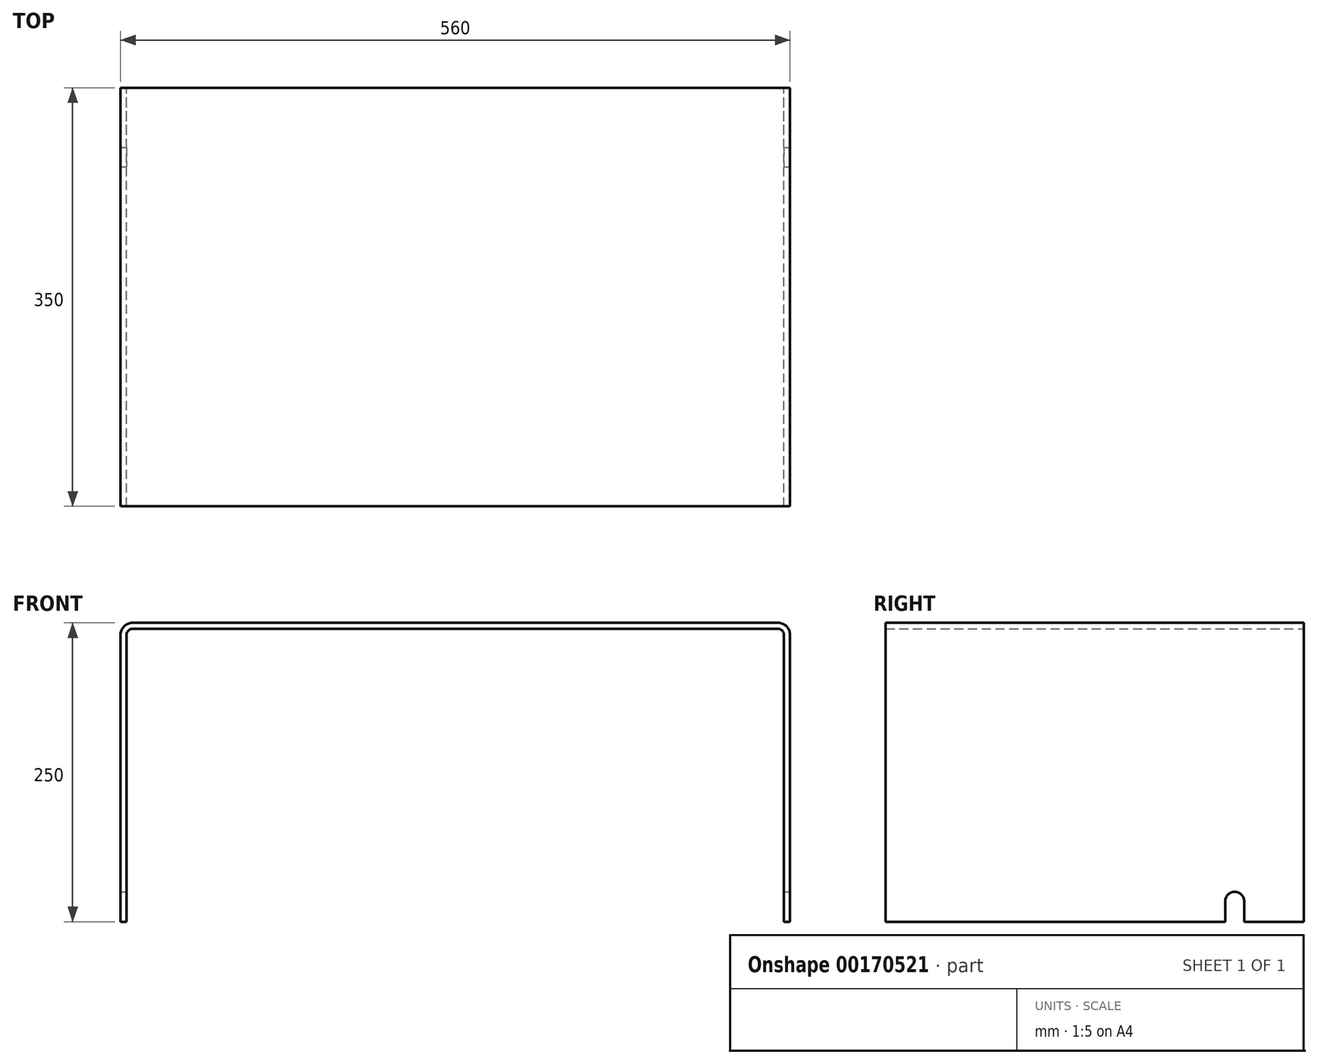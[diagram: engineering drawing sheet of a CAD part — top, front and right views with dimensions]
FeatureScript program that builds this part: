
annotation { "Feature Type Name" : "Feature", "Feature Type Description" : "" }
export const myFeature = defineFeature(function(context is Context, id is Id, definition is map)
    precondition{}
    {
        {
            var Q0;
            Q0=qCreatedBy(makeId("Front.planeOp"),FACE);
            var sketch = newSketch(context, id + "F0", { "sketchPlane" : qUnion([Q0])});
            skLineSegment(sketch, "E0.bottom", {"start": v(-270, 138.08) * mm, "end": v(270, 138.08) * mm});
            skLineSegment(sketch, "E0.top", {"start": v(-280, -111.92) * mm, "end": v(-275, -111.92) * mm});
            skLineSegment(sketch, "E0.left", {"start": v(-280, 128.08) * mm, "end": v(-280, -111.92) * mm});
            skLineSegment(sketch, "E0.right", {"start": v(280, 128.08) * mm, "end": v(280, -111.92) * mm});
            skLineSegment(sketch, "E1", {"start": v(-394.49, 0) * mm, "end": v(397.92, 0) * mm, "construction": true});
            skLineSegment(sketch, "E2", {"start": v(0, 473.58) * mm, "end": v(0, -448.6) * mm, "construction": true});
            skPoint(sketch, "E3.visualSharp", {"position": v(-280, 138.08) * mm});
            skArc(sketch, "E3.filletArc", {"start": v(-270, 138.08) * mm, "mid": v(-277.07, 135.15) * mm, "end": v(-280, 128.08) * mm});
            skPoint(sketch, "E4.visualSharp", {"position": v(280, 138.08) * mm});
            skArc(sketch, "E4.filletArc", {"start": v(280, 128.08) * mm, "mid": v(277.07, 135.15) * mm, "end": v(270, 138.08) * mm});
            skLineSegment(sketch, "E5.0", {"start": v(-275, 128.08) * mm, "end": v(-275, -111.92) * mm});
            skLineSegment(sketch, "E6.0", {"start": v(275, 128.08) * mm, "end": v(275, -111.92) * mm});
            skArc(sketch, "E7.0", {"start": v(275, 128.08) * mm, "mid": v(273.54, 131.62) * mm, "end": v(270, 133.08) * mm});
            skLineSegment(sketch, "E8.0", {"start": v(-270, 133.08) * mm, "end": v(270, 133.08) * mm});
            skArc(sketch, "E9.0", {"start": v(-270, 133.08) * mm, "mid": v(-273.54, 131.62) * mm, "end": v(-275, 128.08) * mm});
            skLineSegment(sketch, "E10.trimOffspring", {"start": v(275, -111.92) * mm, "end": v(280, -111.92) * mm});
            skSolve(sketch);
        }
        {
            var Q0;
            Q0=makeQuery(id+"F0.imprint","IMPRINT",FACE,{"disambiguationData":[TD([[makeQuery(id+"F0.imprint","IMPRINT",EDGE,{"derivedFrom":sQuery(id+"F0.wireOp",EDGE,"E0.bottom")}),-1.0]])]});
            extrude(context, id + "F1", {"entities" : qUnion([Q0]), "depth" : 350 * mm});
        }
        {
            var Q0;
            Q0=makeQuery(id+"F1.opExtrude","SWEPT_FACE",FACE,{"disambiguationData":[OSD([sQuery(id+"F0.wireOp",EDGE,"E0.right")])]});
            var sketch = newSketch(context, id + "F2", { "sketchPlane" : qUnion([Q0])});
            skLineSegment(sketch, "E11", {"start": v(0, -335.58) * mm, "end": v(0, 186.78) * mm, "construction": true});
            skLineSegment(sketch, "E12", {"start": v(-578.66, -111.92) * mm, "end": v(-104.99, -111.92) * mm, "construction": true});
            skLineSegment(sketch, "E13.bottom", {"start": v(-58, -86.92) * mm, "end": v(-58, -86.92) * mm});
            skLineSegment(sketch, "E13.top", {"start": v(-66, -111.92) * mm, "end": v(-50, -111.92) * mm});
            skLineSegment(sketch, "E13.left", {"start": v(-66, -94.92) * mm, "end": v(-66, -111.92) * mm});
            skLineSegment(sketch, "E13.right", {"start": v(-50, -94.92) * mm, "end": v(-50, -111.92) * mm});
            skPoint(sketch, "E14.visualSharp", {"position": v(-66, -86.92) * mm});
            skArc(sketch, "E14.filletArc", {"start": v(-58, -86.92) * mm, "mid": v(-63.66, -89.26) * mm, "end": v(-66, -94.92) * mm});
            skPoint(sketch, "E15.visualSharp", {"position": v(-50, -86.92) * mm});
            skArc(sketch, "E15.filletArc", {"start": v(-50, -94.92) * mm, "mid": v(-52.34, -89.26) * mm, "end": v(-58, -86.92) * mm});
            skSolve(sketch);
        }
        {
            var Q0;
            Q0=makeQuery(id+"F2.imprint","IMPRINT",FACE,{"disambiguationData":[TD([[makeQuery(id+"F2.imprint","IMPRINT",EDGE,{"derivedFrom":sQuery(id+"F2.wireOp",EDGE,"E13.top")}),1.0]])]});
            extrude(context, id + "F3", {"entities" : qUnion([Q0]), "operationType" : NewBodyOperationType.REMOVE, "endBound" : BoundingType.THROUGH_ALL, "oppositeDirection" : true, "depth" : 25 * mm});
        }
    });
